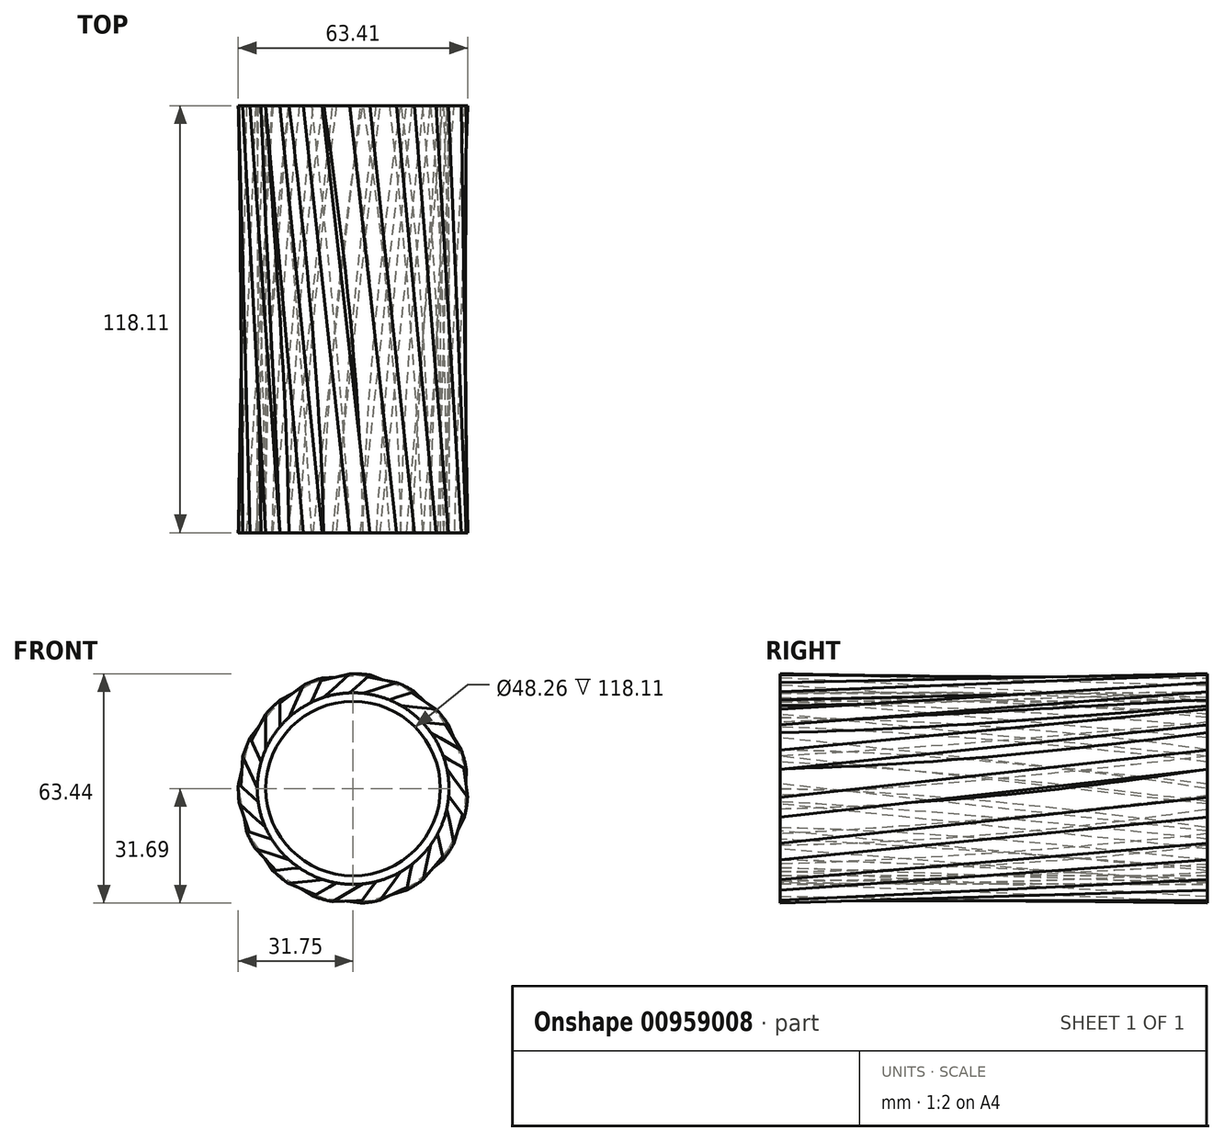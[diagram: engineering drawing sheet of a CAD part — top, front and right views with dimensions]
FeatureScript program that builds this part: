
annotation { "Feature Type Name" : "Feature", "Feature Type Description" : "" }
export const myFeature = defineFeature(function(context is Context, id is Id, definition is map)
    precondition{}
    {
        {
            var Q0;
            Q0=qCreatedBy(makeId("Front.planeOp"),FACE);
            cPlane(context, id + "F0", {"entities" : qUnion([Q0]), "cplaneType" : CPlaneType.OFFSET, "offset" : 118.11 * mm, "width" : 152.4 * mm, "height" : 152.4 * mm});
        }
        {
            var Q0;
            Q0=qCreatedBy(makeId("Front.planeOp"),FACE);
            var sketch = newSketch(context, id + "F1", { "sketchPlane" : qUnion([Q0])});
            skCircle(sketch, "E0", {"center": v(0, 0) * mm, "radius": 31.75 * mm});
            skCircle(sketch, "E1", {"center": v(0, 0) * mm, "radius": 25.4 * mm});
            skLineSegment(sketch, "E2", {"start": v(0, 25.4) * mm, "end": v(12.07, 29.37) * mm});
            skLineSegment(sketch, "E3", {"start": v(8.35, 23.99) * mm, "end": v(16.98, 26.83) * mm});
            skLineSegment(sketch, "E4.1.0", {"start": v(-2.13, 25.31) * mm, "end": v(4.6, 31.41) * mm});
            skLineSegment(sketch, "E4.1.1", {"start": v(-10.33, 23.2) * mm, "end": v(-0.92, 31.74) * mm});
            skLineSegment(sketch, "E4.2.0", {"start": v(-12.24, 22.26) * mm, "end": v(-8.57, 30.57) * mm});
            skLineSegment(sketch, "E4.2.1", {"start": v(-18.88, 17) * mm, "end": v(-13.75, 28.62) * mm});
            skLineSegment(sketch, "E4.3.0", {"start": v(-20.24, 15.35) * mm, "end": v(-20.27, 24.44) * mm});
            skLineSegment(sketch, "E4.3.1", {"start": v(-24.16, 7.85) * mm, "end": v(-24.2, 20.55) * mm});
            skLineSegment(sketch, "E4.4.0", {"start": v(-24.73, 5.8) * mm, "end": v(-28.45, 14.08) * mm});
            skLineSegment(sketch, "E4.4.1", {"start": v(-25.26, -2.66) * mm, "end": v(-30.47, 8.93) * mm});
            skLineSegment(sketch, "E4.5.0", {"start": v(-24.95, -4.76) * mm, "end": v(-31.72, 1.3) * mm});
            skLineSegment(sketch, "E4.5.1", {"start": v(-22, -12.7) * mm, "end": v(-31.47, -4.23) * mm});
            skLineSegment(sketch, "E4.6.0", {"start": v(-20.85, -14.5) * mm, "end": v(-29.5, -11.72) * mm});
            skLineSegment(sketch, "E4.6.1", {"start": v(-14.93, -20.55) * mm, "end": v(-27.03, -16.66) * mm});
            skLineSegment(sketch, "E4.7.0", {"start": v(-13.15, -21.73) * mm, "end": v(-22.19, -22.7) * mm});
            skLineSegment(sketch, "E4.7.1", {"start": v(-5.28, -24.84) * mm, "end": v(-17.91, -26.22) * mm});
            skLineSegment(sketch, "E4.8.0", {"start": v(-3.18, -25.2) * mm, "end": v(-11.03, -29.77) * mm});
            skLineSegment(sketch, "E4.8.1", {"start": v(5.28, -24.84) * mm, "end": v(-5.7, -31.23) * mm});
            skLineSegment(sketch, "E4.9.0", {"start": v(7.35, -24.31) * mm, "end": v(2.03, -31.69) * mm});
            skLineSegment(sketch, "E4.9.1", {"start": v(14.93, -20.55) * mm, "end": v(7.5, -30.85) * mm});
            skLineSegment(sketch, "E4.10.0", {"start": v(16.6, -19.22) * mm, "end": v(14.74, -28.12) * mm});
            skLineSegment(sketch, "E4.10.1", {"start": v(22, -12.7) * mm, "end": v(19.4, -25.14) * mm});
            skLineSegment(sketch, "E4.11.0", {"start": v(22.98, -10.8) * mm, "end": v(24.9, -19.7) * mm});
            skLineSegment(sketch, "E4.11.1", {"start": v(25.26, -2.66) * mm, "end": v(27.94, -15.07) * mm});
            skLineSegment(sketch, "E4.12.0", {"start": v(25.4, -0.53) * mm, "end": v(30.76, -7.86) * mm});
            skLineSegment(sketch, "E4.12.1", {"start": v(24.16, 7.85) * mm, "end": v(31.66, -2.4) * mm});
            skLineSegment(sketch, "E4.13.0", {"start": v(23.41, 9.85) * mm, "end": v(31.3, 5.33) * mm});
            skLineSegment(sketch, "E4.13.1", {"start": v(18.88, 17) * mm, "end": v(29.9, 10.68) * mm});
            skLineSegment(sketch, "E4.14.0", {"start": v(17.38, 18.52) * mm, "end": v(26.43, 17.6) * mm});
            skLineSegment(sketch, "E4.14.1", {"start": v(10.33, 23.2) * mm, "end": v(22.97, 21.92) * mm});
            skCircle(sketch, "E5", {"center": v(0, 0) * mm, "radius": 26.5 * mm});
            skSolve(sketch);
        }
        {
            var Q0;
            Q0=qCreatedBy(id+"F0.planeOp",FACE);
            var sketch = newSketch(context, id + "F2", { "sketchPlane" : qUnion([Q0])});
            skCircle(sketch, "E6", {"center": v(0, 0) * mm, "radius": 31.75 * mm});
            skCircle(sketch, "E7", {"center": v(0, 0) * mm, "radius": 25.4 * mm});
            skLineSegment(sketch, "E8", {"start": v(5.85, 27.32) * mm, "end": v(12.07, 29.37) * mm});
            skLineSegment(sketch, "E9", {"start": v(12.05, 25.2) * mm, "end": v(16.98, 26.83) * mm});
            skLineSegment(sketch, "E10.1.0", {"start": v(0.76, 27.93) * mm, "end": v(4.6, 31.41) * mm});
            skLineSegment(sketch, "E10.1.1", {"start": v(-5.77, 27.34) * mm, "end": v(-0.92, 31.74) * mm});
            skLineSegment(sketch, "E10.2.0", {"start": v(-10.67, 25.82) * mm, "end": v(-8.57, 30.57) * mm});
            skLineSegment(sketch, "E10.2.1", {"start": v(-16.4, 22.63) * mm, "end": v(-13.75, 28.62) * mm});
            skLineSegment(sketch, "E10.3.0", {"start": v(-20.25, 19.25) * mm, "end": v(-20.27, 24.44) * mm});
            skLineSegment(sketch, "E10.3.1", {"start": v(-24.18, 14) * mm, "end": v(-24.2, 20.55) * mm});
            skLineSegment(sketch, "E10.4.0", {"start": v(-26.33, 9.35) * mm, "end": v(-28.45, 14.08) * mm});
            skLineSegment(sketch, "E10.4.1", {"start": v(-27.78, 2.96) * mm, "end": v(-30.47, 8.93) * mm});
            skLineSegment(sketch, "E10.5.0", {"start": v(-27.86, -2.17) * mm, "end": v(-31.72, 1.3) * mm});
            skLineSegment(sketch, "E10.5.1", {"start": v(-26.58, -8.6) * mm, "end": v(-31.47, -4.23) * mm});
            skLineSegment(sketch, "E10.6.0", {"start": v(-24.57, -13.3) * mm, "end": v(-29.5, -11.72) * mm});
            skLineSegment(sketch, "E10.6.1", {"start": v(-20.79, -18.67) * mm, "end": v(-27.03, -16.66) * mm});
            skLineSegment(sketch, "E10.7.0", {"start": v(-17.03, -22.15) * mm, "end": v(-22.19, -22.7) * mm});
            skLineSegment(sketch, "E10.7.1", {"start": v(-11.4, -25.5) * mm, "end": v(-17.91, -26.22) * mm});
            skLineSegment(sketch, "E10.8.0", {"start": v(-6.55, -27.16) * mm, "end": v(-11.03, -29.77) * mm});
            skLineSegment(sketch, "E10.8.1", {"start": v(-0.04, -27.94) * mm, "end": v(-5.7, -31.23) * mm});
            skLineSegment(sketch, "E10.9.0", {"start": v(5.07, -27.48) * mm, "end": v(2.03, -31.69) * mm});
            skLineSegment(sketch, "E10.9.1", {"start": v(11.33, -25.54) * mm, "end": v(7.5, -30.85) * mm});
            skLineSegment(sketch, "E10.10.0", {"start": v(15.8, -23.04) * mm, "end": v(14.74, -28.12) * mm});
            skLineSegment(sketch, "E10.10.1", {"start": v(20.74, -18.72) * mm, "end": v(19.4, -25.14) * mm});
            skLineSegment(sketch, "E10.11.0", {"start": v(23.8, -14.62) * mm, "end": v(24.9, -19.7) * mm});
            skLineSegment(sketch, "E10.11.1", {"start": v(26.56, -8.67) * mm, "end": v(27.94, -15.07) * mm});
            skLineSegment(sketch, "E10.12.0", {"start": v(27.7, -3.67) * mm, "end": v(30.76, -7.86) * mm});
            skLineSegment(sketch, "E10.12.1", {"start": v(27.8, 2.88) * mm, "end": v(31.66, -2.4) * mm});
            skLineSegment(sketch, "E10.13.0", {"start": v(26.8, 7.9) * mm, "end": v(31.3, 5.33) * mm});
            skLineSegment(sketch, "E10.13.1", {"start": v(24.22, 13.94) * mm, "end": v(29.9, 10.68) * mm});
            skLineSegment(sketch, "E10.14.0", {"start": v(21.26, 18.13) * mm, "end": v(26.43, 17.6) * mm});
            skLineSegment(sketch, "E10.14.1", {"start": v(16.45, 22.58) * mm, "end": v(22.97, 21.92) * mm});
            skCircle(sketch, "E11", {"center": v(0, 0) * mm, "radius": 24.13 * mm});
            skPoint(sketch, "E12.orphan", {"position": v(-10.33, 23.2) * mm});
            skPoint(sketch, "E13.orphan", {"position": v(-2.13, 25.31) * mm});
            skPoint(sketch, "E14.orphan", {"position": v(0, 25.4) * mm});
            skPoint(sketch, "E15.orphan", {"position": v(8.35, 23.99) * mm});
            skPoint(sketch, "E16.orphan", {"position": v(10.33, 23.2) * mm});
            skPoint(sketch, "E17.orphan", {"position": v(17.38, 18.52) * mm});
            skPoint(sketch, "E18.orphan", {"position": v(18.88, 17) * mm});
            skPoint(sketch, "E19.orphan", {"position": v(23.41, 9.85) * mm});
            skPoint(sketch, "E20.orphan", {"position": v(24.16, 7.85) * mm});
            skPoint(sketch, "E21.orphan", {"position": v(25.4, -0.53) * mm});
            skPoint(sketch, "E22.orphan", {"position": v(25.26, -2.66) * mm});
            skPoint(sketch, "E23.orphan", {"position": v(22.98, -10.8) * mm});
            skPoint(sketch, "E24.orphan", {"position": v(22, -12.7) * mm});
            skPoint(sketch, "E25.orphan", {"position": v(16.6, -19.22) * mm});
            skPoint(sketch, "E26.orphan", {"position": v(14.93, -20.55) * mm});
            skPoint(sketch, "E27.orphan", {"position": v(7.35, -24.31) * mm});
            skPoint(sketch, "E28.orphan", {"position": v(5.28, -24.84) * mm});
            skPoint(sketch, "E29.orphan", {"position": v(-3.18, -25.2) * mm});
            skPoint(sketch, "E30.orphan", {"position": v(-5.28, -24.84) * mm});
            skPoint(sketch, "E31.orphan", {"position": v(-13.15, -21.73) * mm});
            skPoint(sketch, "E32.orphan", {"position": v(-14.93, -20.55) * mm});
            skPoint(sketch, "E33.orphan", {"position": v(-20.85, -14.5) * mm});
            skPoint(sketch, "E34.orphan", {"position": v(-22, -12.7) * mm});
            skPoint(sketch, "E35.orphan", {"position": v(-24.95, -4.76) * mm});
            skPoint(sketch, "E36.orphan", {"position": v(-25.26, -2.66) * mm});
            skPoint(sketch, "E37.orphan", {"position": v(-24.73, 5.8) * mm});
            skPoint(sketch, "E38.orphan", {"position": v(-24.16, 7.85) * mm});
            skPoint(sketch, "E39.orphan", {"position": v(-20.24, 15.35) * mm});
            skPoint(sketch, "E40.orphan", {"position": v(-18.88, 17) * mm});
            skPoint(sketch, "E41.orphan", {"position": v(-12.24, 22.26) * mm});
            skCircle(sketch, "E42", {"center": v(0, 0) * mm, "radius": 26.5 * mm});
            skLineSegment(sketch, "E43", {"start": v(16.45, 22.58) * mm, "end": v(13.28, 22.92) * mm});
            skLineSegment(sketch, "E44", {"start": v(21.26, 18.13) * mm, "end": v(19.09, 18.37) * mm});
            skLineSegment(sketch, "E45.1.0", {"start": v(5.85, 27.32) * mm, "end": v(2.81, 26.34) * mm});
            skLineSegment(sketch, "E45.1.1", {"start": v(12.05, 25.2) * mm, "end": v(9.96, 24.55) * mm});
            skLineSegment(sketch, "E45.2.0", {"start": v(-5.77, 27.34) * mm, "end": v(-8.14, 25.2) * mm});
            skLineSegment(sketch, "E45.2.1", {"start": v(0.76, 27.93) * mm, "end": v(-0.88, 26.48) * mm});
            skLineSegment(sketch, "E45.3.0", {"start": v(-16.4, 22.63) * mm, "end": v(-17.7, 19.72) * mm});
            skLineSegment(sketch, "E45.3.1", {"start": v(-10.67, 25.82) * mm, "end": v(-11.57, 23.83) * mm});
            skLineSegment(sketch, "E45.4.0", {"start": v(-24.18, 14) * mm, "end": v(-24.18, 10.82) * mm});
            skLineSegment(sketch, "E45.4.1", {"start": v(-20.25, 19.25) * mm, "end": v(-20.27, 17.06) * mm});
            skLineSegment(sketch, "E45.5.0", {"start": v(-27.78, 2.96) * mm, "end": v(-26.5, 0.05) * mm});
            skLineSegment(sketch, "E45.5.1", {"start": v(-26.33, 9.35) * mm, "end": v(-25.45, 7.34) * mm});
            skLineSegment(sketch, "E45.6.0", {"start": v(-26.58, -8.6) * mm, "end": v(-24.22, -10.73) * mm});
            skLineSegment(sketch, "E45.6.1", {"start": v(-27.86, -2.17) * mm, "end": v(-26.24, -3.64) * mm});
            skLineSegment(sketch, "E45.7.0", {"start": v(-20.79, -18.67) * mm, "end": v(-17.76, -19.66) * mm});
            skLineSegment(sketch, "E45.7.1", {"start": v(-24.57, -13.3) * mm, "end": v(-22.49, -14) * mm});
            skLineSegment(sketch, "E45.8.0", {"start": v(-11.4, -25.5) * mm, "end": v(-8.23, -25.18) * mm});
            skLineSegment(sketch, "E45.8.1", {"start": v(-17.03, -22.15) * mm, "end": v(-14.85, -21.94) * mm});
            skLineSegment(sketch, "E45.9.0", {"start": v(-0.04, -27.94) * mm, "end": v(2.72, -26.35) * mm});
            skLineSegment(sketch, "E45.9.1", {"start": v(-6.55, -27.16) * mm, "end": v(-4.64, -26.08) * mm});
            skLineSegment(sketch, "E45.10.0", {"start": v(11.33, -25.54) * mm, "end": v(13.2, -22.96) * mm});
            skLineSegment(sketch, "E45.10.1", {"start": v(5.07, -27.48) * mm, "end": v(6.37, -25.71) * mm});
            skLineSegment(sketch, "E45.11.0", {"start": v(20.74, -18.72) * mm, "end": v(21.4, -15.6) * mm});
            skLineSegment(sketch, "E45.11.1", {"start": v(15.8, -23.04) * mm, "end": v(16.28, -20.9) * mm});
            skLineSegment(sketch, "E45.12.0", {"start": v(26.56, -8.67) * mm, "end": v(25.9, -5.55) * mm});
            skLineSegment(sketch, "E45.12.1", {"start": v(23.8, -14.62) * mm, "end": v(23.37, -12.48) * mm});
            skLineSegment(sketch, "E45.13.0", {"start": v(27.8, 2.88) * mm, "end": v(25.92, 5.46) * mm});
            skLineSegment(sketch, "E45.13.1", {"start": v(27.7, -3.67) * mm, "end": v(26.42, -1.9) * mm});
            skLineSegment(sketch, "E45.14.0", {"start": v(24.22, 13.94) * mm, "end": v(21.46, 15.53) * mm});
            skLineSegment(sketch, "E45.14.1", {"start": v(26.8, 7.9) * mm, "end": v(24.9, 9.02) * mm});
            skSolve(sketch);
        }
        {
            var Q0;
            {var subQ0=sQuery(id+"F1.wireOp",EDGE,"E4.13.0");Q0=makeQuery(id+"F1.imprint","IMPRINT",FACE,{"disambiguationData":[TD([[makeQuery(id+"F1.imprint","IMPRINT",EDGE,{"derivedFrom":subQ0}),1.0]])]});}
            var Q1;
            {var subQ0=sQuery(id+"F2.wireOp",EDGE,"E10.12.0");Q1=makeQuery(id+"F2.imprint","IMPRINT",FACE,{"disambiguationData":[TD([[makeQuery(id+"F2.imprint","IMPRINT",EDGE,{"derivedFrom":subQ0}),1.0]])]});}
            loft(context, id + "F3", {"sheetProfilesArray" : [{ "sheetProfileEntities" : qUnion([Q0]) }, { "sheetProfileEntities" : qUnion([Q1]) }]});
        }
        {
            var Q0;
            {var subQ0=sQuery(id+"F1.wireOp",EDGE,"E4.12.0");Q0=makeQuery(id+"F1.imprint","IMPRINT",FACE,{"disambiguationData":[TD([[makeQuery(id+"F1.imprint","IMPRINT",EDGE,{"derivedFrom":subQ0}),1.0]])]});}
            var Q1;
            {var subQ0=sQuery(id+"F2.wireOp",EDGE,"E10.11.0");Q1=makeQuery(id+"F2.imprint","IMPRINT",FACE,{"disambiguationData":[TD([[makeQuery(id+"F2.imprint","IMPRINT",EDGE,{"derivedFrom":subQ0}),1.0]])]});}
            loft(context, id + "F4", {"sheetProfilesArray" : [{ "sheetProfileEntities" : qUnion([Q0]) }, { "sheetProfileEntities" : qUnion([Q1]) }]});
        }
        {
            var Q1;
            {var subQ0=sQuery(id+"F2.wireOp",EDGE,"E10.10.0");Q1=makeQuery(id+"F2.imprint","IMPRINT",FACE,{"disambiguationData":[TD([[makeQuery(id+"F2.imprint","IMPRINT",EDGE,{"derivedFrom":subQ0}),1.0]])]});}
            var Q2;
            {var subQ0=sQuery(id+"F1.wireOp",EDGE,"E4.11.0");Q2=makeQuery(id+"F1.imprint","IMPRINT",FACE,{"disambiguationData":[TD([[makeQuery(id+"F1.imprint","IMPRINT",EDGE,{"derivedFrom":subQ0}),1.0]])]});}
            loft(context, id + "F5", {"operationType" : NewBodyOperationType.ADD, "sheetProfilesArray" : [{ "sheetProfileEntities" : qUnion([Q1]) }, { "sheetProfileEntities" : qUnion([Q2]) }]});
        }
        {
            var Q1;
            {var subQ0=sQuery(id+"F2.wireOp",EDGE,"E10.9.0");Q1=makeQuery(id+"F2.imprint","IMPRINT",FACE,{"disambiguationData":[TD([[makeQuery(id+"F2.imprint","IMPRINT",EDGE,{"derivedFrom":subQ0}),1.0]])]});}
            var Q2;
            {var subQ0=sQuery(id+"F1.wireOp",EDGE,"E4.10.0");Q2=makeQuery(id+"F1.imprint","IMPRINT",FACE,{"disambiguationData":[TD([[makeQuery(id+"F1.imprint","IMPRINT",EDGE,{"derivedFrom":subQ0}),1.0]])]});}
            loft(context, id + "F6", {"operationType" : NewBodyOperationType.ADD, "sheetProfilesArray" : [{ "sheetProfileEntities" : qUnion([Q1]) }, { "sheetProfileEntities" : qUnion([Q2]) }]});
        }
        {
            var Q1;
            {var subQ0=sQuery(id+"F2.wireOp",EDGE,"E10.8.0");Q1=makeQuery(id+"F2.imprint","IMPRINT",FACE,{"disambiguationData":[TD([[makeQuery(id+"F2.imprint","IMPRINT",EDGE,{"derivedFrom":subQ0}),1.0]])]});}
            var Q2;
            {var subQ0=sQuery(id+"F1.wireOp",EDGE,"E4.9.0");Q2=makeQuery(id+"F1.imprint","IMPRINT",FACE,{"disambiguationData":[TD([[makeQuery(id+"F1.imprint","IMPRINT",EDGE,{"derivedFrom":subQ0}),1.0]])]});}
            loft(context, id + "F7", {"operationType" : NewBodyOperationType.ADD, "sheetProfilesArray" : [{ "sheetProfileEntities" : qUnion([Q1]) }, { "sheetProfileEntities" : qUnion([Q2]) }]});
        }
        {
            var Q1;
            {var subQ0=sQuery(id+"F2.wireOp",EDGE,"E10.7.0");Q1=makeQuery(id+"F2.imprint","IMPRINT",FACE,{"disambiguationData":[TD([[makeQuery(id+"F2.imprint","IMPRINT",EDGE,{"derivedFrom":subQ0}),1.0]])]});}
            var Q2;
            {var subQ0=sQuery(id+"F1.wireOp",EDGE,"E4.8.0");Q2=makeQuery(id+"F1.imprint","IMPRINT",FACE,{"disambiguationData":[TD([[makeQuery(id+"F1.imprint","IMPRINT",EDGE,{"derivedFrom":subQ0}),1.0]])]});}
            loft(context, id + "F8", {"operationType" : NewBodyOperationType.ADD, "sheetProfilesArray" : [{ "sheetProfileEntities" : qUnion([Q1]) }, { "sheetProfileEntities" : qUnion([Q2]) }]});
        }
        {
            var Q1;
            {var subQ0=sQuery(id+"F1.wireOp",EDGE,"E4.7.0");Q1=makeQuery(id+"F1.imprint","IMPRINT",FACE,{"disambiguationData":[TD([[makeQuery(id+"F1.imprint","IMPRINT",EDGE,{"derivedFrom":subQ0}),1.0]])]});}
            var Q2;
            {var subQ0=sQuery(id+"F2.wireOp",EDGE,"E10.6.0");Q2=makeQuery(id+"F2.imprint","IMPRINT",FACE,{"disambiguationData":[TD([[makeQuery(id+"F2.imprint","IMPRINT",EDGE,{"derivedFrom":subQ0}),1.0]])]});}
            loft(context, id + "F9", {"operationType" : NewBodyOperationType.ADD, "sheetProfilesArray" : [{ "sheetProfileEntities" : qUnion([Q1]) }, { "sheetProfileEntities" : qUnion([Q2]) }]});
        }
        {
            var Q1;
            {var subQ0=sQuery(id+"F1.wireOp",EDGE,"E4.6.0");Q1=makeQuery(id+"F1.imprint","IMPRINT",FACE,{"disambiguationData":[TD([[makeQuery(id+"F1.imprint","IMPRINT",EDGE,{"derivedFrom":subQ0}),1.0]])]});}
            var Q2;
            {var subQ0=sQuery(id+"F2.wireOp",EDGE,"E10.5.0");Q2=makeQuery(id+"F2.imprint","IMPRINT",FACE,{"disambiguationData":[TD([[makeQuery(id+"F2.imprint","IMPRINT",EDGE,{"derivedFrom":subQ0}),1.0]])]});}
            loft(context, id + "F10", {"operationType" : NewBodyOperationType.ADD, "sheetProfilesArray" : [{ "sheetProfileEntities" : qUnion([Q1]) }, { "sheetProfileEntities" : qUnion([Q2]) }]});
        }
        {
            var Q1;
            {var subQ0=sQuery(id+"F1.wireOp",EDGE,"E4.5.0");Q1=makeQuery(id+"F1.imprint","IMPRINT",FACE,{"disambiguationData":[TD([[makeQuery(id+"F1.imprint","IMPRINT",EDGE,{"derivedFrom":subQ0}),1.0]])]});}
            var Q2;
            {var subQ0=sQuery(id+"F2.wireOp",EDGE,"E10.4.0");Q2=makeQuery(id+"F2.imprint","IMPRINT",FACE,{"disambiguationData":[TD([[makeQuery(id+"F2.imprint","IMPRINT",EDGE,{"derivedFrom":subQ0}),1.0]])]});}
            loft(context, id + "F11", {"operationType" : NewBodyOperationType.ADD, "sheetProfilesArray" : [{ "sheetProfileEntities" : qUnion([Q1]) }, { "sheetProfileEntities" : qUnion([Q2]) }]});
        }
        {
            var Q1;
            {var subQ0=sQuery(id+"F1.wireOp",EDGE,"E4.4.0");Q1=makeQuery(id+"F1.imprint","IMPRINT",FACE,{"disambiguationData":[TD([[makeQuery(id+"F1.imprint","IMPRINT",EDGE,{"derivedFrom":subQ0}),1.0]])]});}
            var Q2;
            {var subQ0=sQuery(id+"F2.wireOp",EDGE,"E10.3.0");Q2=makeQuery(id+"F2.imprint","IMPRINT",FACE,{"disambiguationData":[TD([[makeQuery(id+"F2.imprint","IMPRINT",EDGE,{"derivedFrom":subQ0}),1.0]])]});}
            loft(context, id + "F12", {"operationType" : NewBodyOperationType.ADD, "sheetProfilesArray" : [{ "sheetProfileEntities" : qUnion([Q1]) }, { "sheetProfileEntities" : qUnion([Q2]) }]});
        }
        {
            var Q1;
            {var subQ0=sQuery(id+"F1.wireOp",EDGE,"E4.3.0");Q1=makeQuery(id+"F1.imprint","IMPRINT",FACE,{"disambiguationData":[TD([[makeQuery(id+"F1.imprint","IMPRINT",EDGE,{"derivedFrom":subQ0}),1.0]])]});}
            var Q2;
            {var subQ0=sQuery(id+"F2.wireOp",EDGE,"E10.2.0");Q2=makeQuery(id+"F2.imprint","IMPRINT",FACE,{"disambiguationData":[TD([[makeQuery(id+"F2.imprint","IMPRINT",EDGE,{"derivedFrom":subQ0}),1.0]])]});}
            loft(context, id + "F13", {"operationType" : NewBodyOperationType.ADD, "sheetProfilesArray" : [{ "sheetProfileEntities" : qUnion([Q1]) }, { "sheetProfileEntities" : qUnion([Q2]) }]});
        }
        {
            var Q1;
            {var subQ0=sQuery(id+"F2.wireOp",EDGE,"E10.1.0");Q1=makeQuery(id+"F2.imprint","IMPRINT",FACE,{"disambiguationData":[TD([[makeQuery(id+"F2.imprint","IMPRINT",EDGE,{"derivedFrom":subQ0}),1.0]])]});}
            var Q2;
            {var subQ0=sQuery(id+"F1.wireOp",EDGE,"E4.2.0");Q2=makeQuery(id+"F1.imprint","IMPRINT",FACE,{"disambiguationData":[TD([[makeQuery(id+"F1.imprint","IMPRINT",EDGE,{"derivedFrom":subQ0}),1.0]])]});}
            loft(context, id + "F14", {"operationType" : NewBodyOperationType.ADD, "sheetProfilesArray" : [{ "sheetProfileEntities" : qUnion([Q1]) }, { "sheetProfileEntities" : qUnion([Q2]) }]});
        }
        {
            var Q1;
            {var subQ0=sQuery(id+"F2.wireOp",EDGE,"E8");Q1=makeQuery(id+"F2.imprint","IMPRINT",FACE,{"disambiguationData":[TD([[makeQuery(id+"F2.imprint","IMPRINT",EDGE,{"derivedFrom":subQ0}),-1.0]])]});}
            var Q2;
            {var subQ0=sQuery(id+"F1.wireOp",EDGE,"E4.1.0");Q2=makeQuery(id+"F1.imprint","IMPRINT",FACE,{"disambiguationData":[TD([[makeQuery(id+"F1.imprint","IMPRINT",EDGE,{"derivedFrom":subQ0}),1.0]])]});}
            loft(context, id + "F15", {"operationType" : NewBodyOperationType.ADD, "sheetProfilesArray" : [{ "sheetProfileEntities" : qUnion([Q1]) }, { "sheetProfileEntities" : qUnion([Q2]) }]});
        }
        {
            var Q1;
            {var subQ0=sQuery(id+"F2.wireOp",EDGE,"E10.14.0");Q1=makeQuery(id+"F2.imprint","IMPRINT",FACE,{"disambiguationData":[TD([[makeQuery(id+"F2.imprint","IMPRINT",EDGE,{"derivedFrom":subQ0}),1.0]])]});}
            var Q2;
            {var subQ0=sQuery(id+"F1.wireOp",EDGE,"E2");Q2=makeQuery(id+"F1.imprint","IMPRINT",FACE,{"disambiguationData":[TD([[makeQuery(id+"F1.imprint","IMPRINT",EDGE,{"derivedFrom":subQ0}),-1.0]])]});}
            loft(context, id + "F16", {"operationType" : NewBodyOperationType.ADD, "sheetProfilesArray" : [{ "sheetProfileEntities" : qUnion([Q1]) }, { "sheetProfileEntities" : qUnion([Q2]) }]});
        }
        {
            var Q1;
            {var subQ0=sQuery(id+"F2.wireOp",EDGE,"E10.13.0");Q1=makeQuery(id+"F2.imprint","IMPRINT",FACE,{"disambiguationData":[TD([[makeQuery(id+"F2.imprint","IMPRINT",EDGE,{"derivedFrom":subQ0}),1.0]])]});}
            var Q2;
            {var subQ0=sQuery(id+"F1.wireOp",EDGE,"E4.14.0");Q2=makeQuery(id+"F1.imprint","IMPRINT",FACE,{"disambiguationData":[TD([[makeQuery(id+"F1.imprint","IMPRINT",EDGE,{"derivedFrom":subQ0}),1.0]])]});}
            loft(context, id + "F17", {"operationType" : NewBodyOperationType.ADD, "sheetProfilesArray" : [{ "sheetProfileEntities" : qUnion([Q1]) }, { "sheetProfileEntities" : qUnion([Q2]) }]});
        }
        {
            var Q0;
            Q0=makeQuery(id+"F2.imprint","IMPRINT",FACE,{"disambiguationData":[TD([[makeQuery(id+"F2.imprint","IMPRINT",EDGE,{"derivedFrom":sQuery(id+"F2.wireOp",EDGE,"E7")}),-1.0]])]});
            var Q1;
            Q1=makeQuery(id+"F2.imprint","IMPRINT",FACE,{"disambiguationData":[TD([[makeQuery(id+"F2.imprint","IMPRINT",EDGE,{"derivedFrom":sQuery(id+"F2.wireOp",EDGE,"E7")}),1.0]])]});
            extrude(context, id + "F18", {"entities" : qUnion([Q0, Q1]), "operationType" : NewBodyOperationType.ADD, "oppositeDirection" : true, "depth" : 118.11 * mm, "offsetDistance" : 25.4 * mm});
        }
    });
